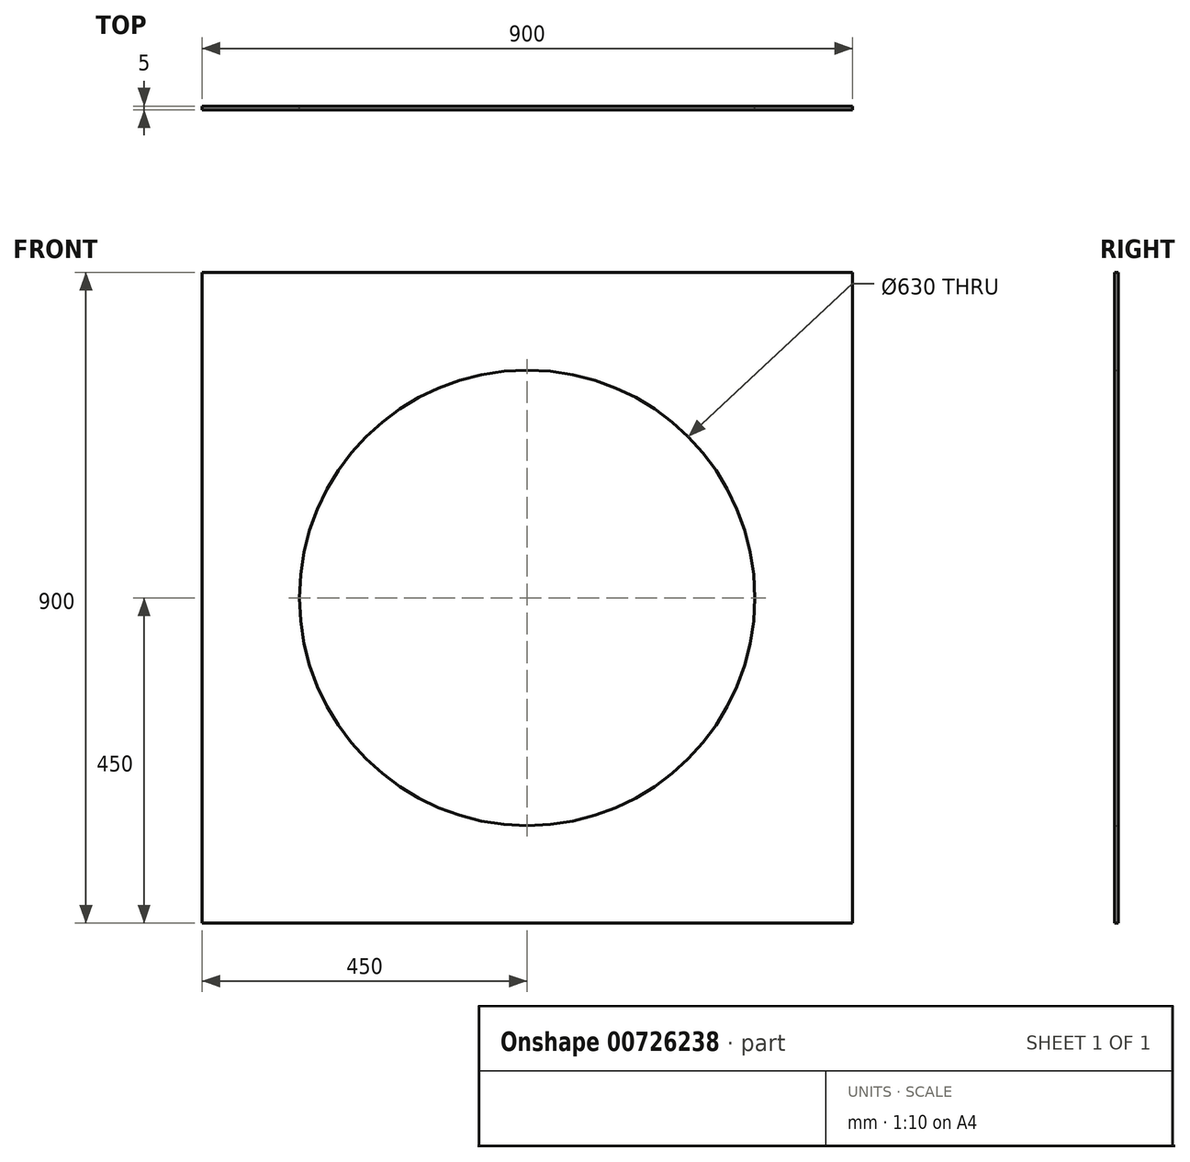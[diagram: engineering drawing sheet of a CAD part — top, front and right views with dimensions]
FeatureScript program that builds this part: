
annotation { "Feature Type Name" : "Feature", "Feature Type Description" : "" }
export const myFeature = defineFeature(function(context is Context, id is Id, definition is map)
    precondition{}
    {
        {
            var Q0;
            Q0=qCreatedBy(makeId("Front.planeOp"),FACE);
            var sketch = newSketch(context, id + "F0", { "sketchPlane" : qUnion([Q0])});
            skCircle(sketch, "E0", {"center": v(0, 0) * mm, "radius": 315 * mm});
            skLineSegment(sketch, "E1.bottom", {"start": v(-450, 450) * mm, "end": v(450, 450) * mm});
            skLineSegment(sketch, "E1.top", {"start": v(-450, -450) * mm, "end": v(450, -450) * mm});
            skLineSegment(sketch, "E1.left", {"start": v(-450, 450) * mm, "end": v(-450, -450) * mm});
            skLineSegment(sketch, "E1.right", {"start": v(450, 450) * mm, "end": v(450, -450) * mm});
            skSolve(sketch);
        }
        {
            var Q0;
            Q0=makeQuery(id+"F0.imprint","IMPRINT",FACE,{"disambiguationData":[TD([[makeQuery(id+"F0.imprint","IMPRINT",EDGE,{"derivedFrom":sQuery(id+"F0.wireOp",EDGE,"E0")}),-1.0]])]});
            extrude(context, id + "F1", {"entities" : qUnion([Q0]), "depth" : 5 * mm, "offsetDistance" : 25 * mm});
        }
    });
